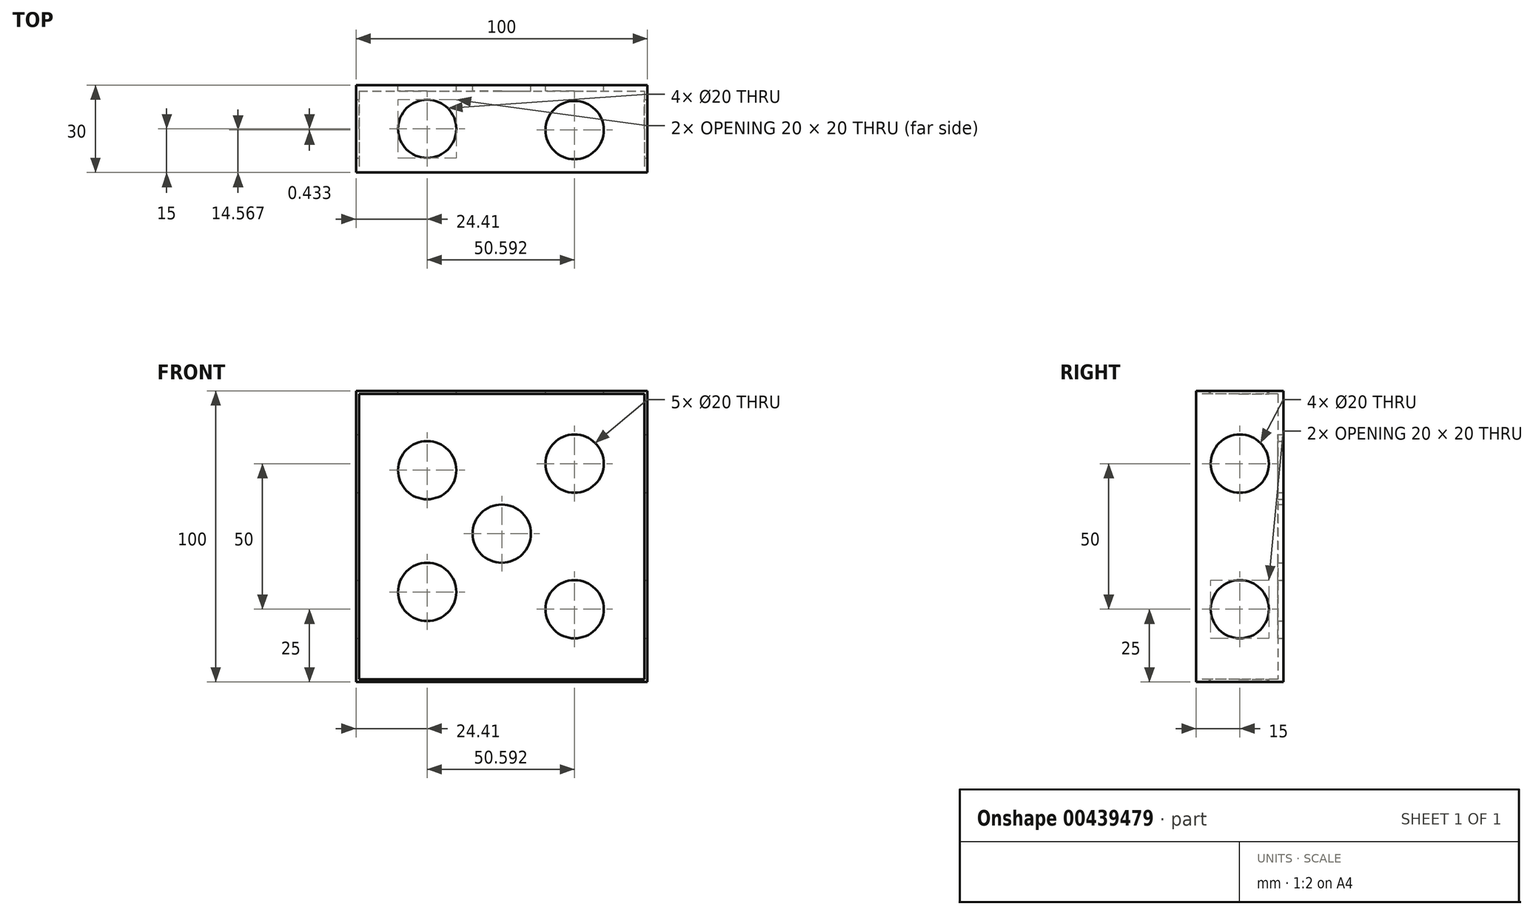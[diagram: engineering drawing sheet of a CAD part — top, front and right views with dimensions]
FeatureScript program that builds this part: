
annotation { "Feature Type Name" : "Feature", "Feature Type Description" : "" }
export const myFeature = defineFeature(function(context is Context, id is Id, definition is map)
    precondition{}
    {
        {
            var Q0;
            Q0=qCreatedBy(makeId("Front.planeOp"),FACE);
            var sketch = newSketch(context, id + "F0", { "sketchPlane" : qUnion([Q0])});
            skLineSegment(sketch, "E0.bottom", {"start": v(-24.4, 49.04) * mm, "end": v(75.6, 49.04) * mm});
            skLineSegment(sketch, "E0.top", {"start": v(-24.4, -50.96) * mm, "end": v(75.6, -50.96) * mm});
            skLineSegment(sketch, "E0.left", {"start": v(-24.4, 49.04) * mm, "end": v(-24.4, -50.96) * mm});
            skLineSegment(sketch, "E0.right", {"start": v(75.6, 49.04) * mm, "end": v(75.6, -50.96) * mm});
            skSolve(sketch);
        }
        {
            var Q0;
            Q0=makeQuery(id+"F0.imprint","IMPRINT",FACE,{"disambiguationData":[TD([[makeQuery(id+"F0.imprint","IMPRINT",EDGE,{"derivedFrom":sQuery(id+"F0.wireOp",EDGE,"E0.bottom")}),-1.0]])]});
            var Q1;
            Q1 = qSketchRegion(id + "F2", true);
            extrude(context, id + "F1", {"entities" : qUnion([Q0, Q1]), "oppositeDirection" : true, "depth" : 30 * mm});
        }
        {
            var Q0;
            Q0=makeQuery(id+"F1.opExtrude","SWEPT_FACE",FACE,{"disambiguationData":[OSD([sQuery(id+"F0.wireOp",EDGE,"E0.right")])]});
            var sketch = newSketch(context, id + "F2", { "sketchPlane" : qUnion([Q0])});
            skCircle(sketch, "E1", {"center": v(15, 24.04) * mm, "radius": 10 * mm});
            skCircle(sketch, "E2", {"center": v(15, -25.96) * mm, "radius": 10 * mm});
            skSolve(sketch);
        }
        {
            var Q0;
            Q0=makeQuery(id+"F2.imprint","IMPRINT",FACE,{"disambiguationData":[TD([[makeQuery(id+"F2.imprint","IMPRINT",EDGE,{"derivedFrom":sQuery(id+"F2.wireOp",EDGE,"E1")}),1.0]])]});
            var Q1;
            Q1=makeQuery(id+"F2.imprint","IMPRINT",FACE,{"disambiguationData":[TD([[makeQuery(id+"F2.imprint","IMPRINT",EDGE,{"derivedFrom":sQuery(id+"F2.wireOp",EDGE,"E2")}),1.0]])]});
            extrude(context, id + "F3", {"entities" : qUnion([Q0, Q1]), "operationType" : NewBodyOperationType.REMOVE, "oppositeDirection" : true, "depth" : 100 * mm});
        }
        {
            var Q0;
            Q0=makeQuery(id+"F1.opExtrude","SWEPT_FACE",FACE,{"disambiguationData":[OSD([sQuery(id+"F0.wireOp",EDGE,"E0.bottom")])]});
            var sketch = newSketch(context, id + "F4", { "sketchPlane" : qUnion([Q0])});
            skCircle(sketch, "E3", {"center": v(0, 15) * mm, "radius": 10 * mm});
            skCircle(sketch, "E4", {"center": v(50.6, 14.57) * mm, "radius": 10 * mm});
            skSolve(sketch);
        }
        {
            var Q0;
            Q0 = qSketchRegion(id + "F4", true);
            extrude(context, id + "F5", {"entities" : qUnion([Q0]), "operationType" : NewBodyOperationType.REMOVE, "oppositeDirection" : true, "depth" : 100 * mm});
        }
        {
            var Q0;
            Q0=makeQuery(id+"F1.opExtrude","CAP_FACE",FACE,{"disambiguationData":[OSD([sQuery(id+"F0.wireOp",EDGE,"E0.bottom"),sQuery(id+"F0.wireOp",EDGE,"E0.top"),sQuery(id+"F0.wireOp",EDGE,"E0.left"),sQuery(id+"F0.wireOp",EDGE,"E0.right")])],"isStart":true});
            var sketch = newSketch(context, id + "F6", { "sketchPlane" : qUnion([Q0])});
            skLineSegment(sketch, "E5.bottom", {"start": v(-23.4, 47.93) * mm, "end": v(74.6, 47.93) * mm});
            skLineSegment(sketch, "E5.top", {"start": v(-23.4, -50.07) * mm, "end": v(74.6, -50.07) * mm});
            skLineSegment(sketch, "E5.left", {"start": v(-23.4, 47.93) * mm, "end": v(-23.4, -50.07) * mm});
            skLineSegment(sketch, "E5.right", {"start": v(74.6, 47.93) * mm, "end": v(74.6, -50.07) * mm});
            skSolve(sketch);
        }
        {
            var Q0;
            Q0=makeQuery(id+"F6.imprint","IMPRINT",FACE,{"disambiguationData":[TD([[makeQuery(id+"F6.imprint","IMPRINT",EDGE,{"derivedFrom":sQuery(id+"F6.wireOp",EDGE,"E5.bottom")}),-1.0]])]});
            extrude(context, id + "F7", {"entities" : qUnion([Q0]), "operationType" : NewBodyOperationType.REMOVE, "oppositeDirection" : true, "depth" : 28 * mm});
        }
        {
            var Q0;
            Q0=makeQuery(id+"F1.opExtrude","CAP_FACE",FACE,{"disambiguationData":[OSD([sQuery(id+"F0.wireOp",EDGE,"E0.bottom"),sQuery(id+"F0.wireOp",EDGE,"E0.top"),sQuery(id+"F0.wireOp",EDGE,"E0.left"),sQuery(id+"F0.wireOp",EDGE,"E0.right")])],"isStart":false});
            var sketch = newSketch(context, id + "F8", { "sketchPlane" : qUnion([Q0])});
            skCircle(sketch, "E6", {"center": v(0, 21.8) * mm, "radius": 10 * mm});
            skCircle(sketch, "E7", {"center": v(0, -20.04) * mm, "radius": 10 * mm});
            skCircle(sketch, "E8", {"center": v(-50.6, 24.04) * mm, "radius": 10 * mm});
            skCircle(sketch, "E9", {"center": v(-50.6, -25.96) * mm, "radius": 10 * mm});
            skCircle(sketch, "E10", {"center": v(-25.6, 0) * mm, "radius": 10 * mm});
            skSolve(sketch);
        }
        {
            var Q0;
            Q0=makeQuery(id+"F8.imprint","IMPRINT",FACE,{"disambiguationData":[TD([[makeQuery(id+"F8.imprint","IMPRINT",EDGE,{"derivedFrom":sQuery(id+"F8.wireOp",EDGE,"E7")}),1.0]])]});
            var Q1;
            Q1=makeQuery(id+"F8.imprint","IMPRINT",FACE,{"disambiguationData":[TD([[makeQuery(id+"F8.imprint","IMPRINT",EDGE,{"derivedFrom":sQuery(id+"F8.wireOp",EDGE,"E6")}),1.0]])]});
            var Q2;
            Q2=makeQuery(id+"F8.imprint","IMPRINT",FACE,{"disambiguationData":[TD([[makeQuery(id+"F8.imprint","IMPRINT",EDGE,{"derivedFrom":sQuery(id+"F8.wireOp",EDGE,"E10")}),1.0]])]});
            var Q3;
            Q3=makeQuery(id+"F8.imprint","IMPRINT",FACE,{"disambiguationData":[TD([[makeQuery(id+"F8.imprint","IMPRINT",EDGE,{"derivedFrom":sQuery(id+"F8.wireOp",EDGE,"E8")}),1.0]])]});
            var Q4;
            Q4=makeQuery(id+"F8.imprint","IMPRINT",FACE,{"disambiguationData":[TD([[makeQuery(id+"F8.imprint","IMPRINT",EDGE,{"derivedFrom":sQuery(id+"F8.wireOp",EDGE,"E9")}),1.0]])]});
            extrude(context, id + "F9", {"entities" : qUnion([Q0, Q1, Q2, Q3, Q4]), "operationType" : NewBodyOperationType.REMOVE, "oppositeDirection" : true, "depth" : 3 * mm});
        }
    });
